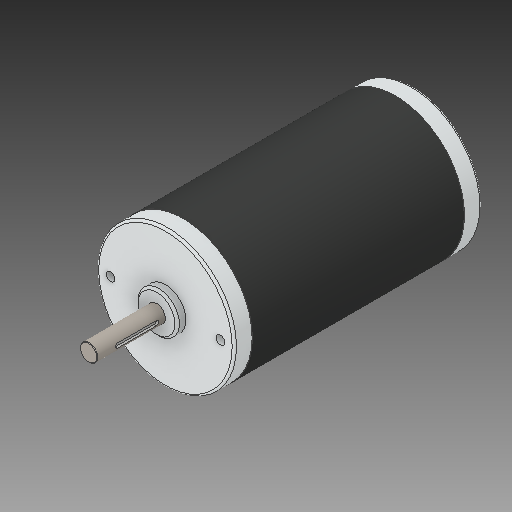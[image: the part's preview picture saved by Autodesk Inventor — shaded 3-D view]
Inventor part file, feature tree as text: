
AUTODESK INVENTOR PART (.ipt)
format: ipt  version: 2017 (Build 210142000, 142)  size: 178,176 bytes
history: native  units: in
note: dims shown in document units (in); Inventor stores cm internally (conversion verified against a paired STEP export)
features: fillet x1
ambient origin geometry x8: Origin, YZ Plane, XZ Plane, XY Plane, X Axis, Y Axis, Z Axis, Center Point
bodies: Solid1 (feature_tree)
feature tree (1):
  fillet  "Fillet5"  [1 undecoded]
note: 1 required parameter value undecoded (feature->parameter linkage not recoverable at this tier; creation-order binding heuristic only, values carry confidence <= 0.55)
